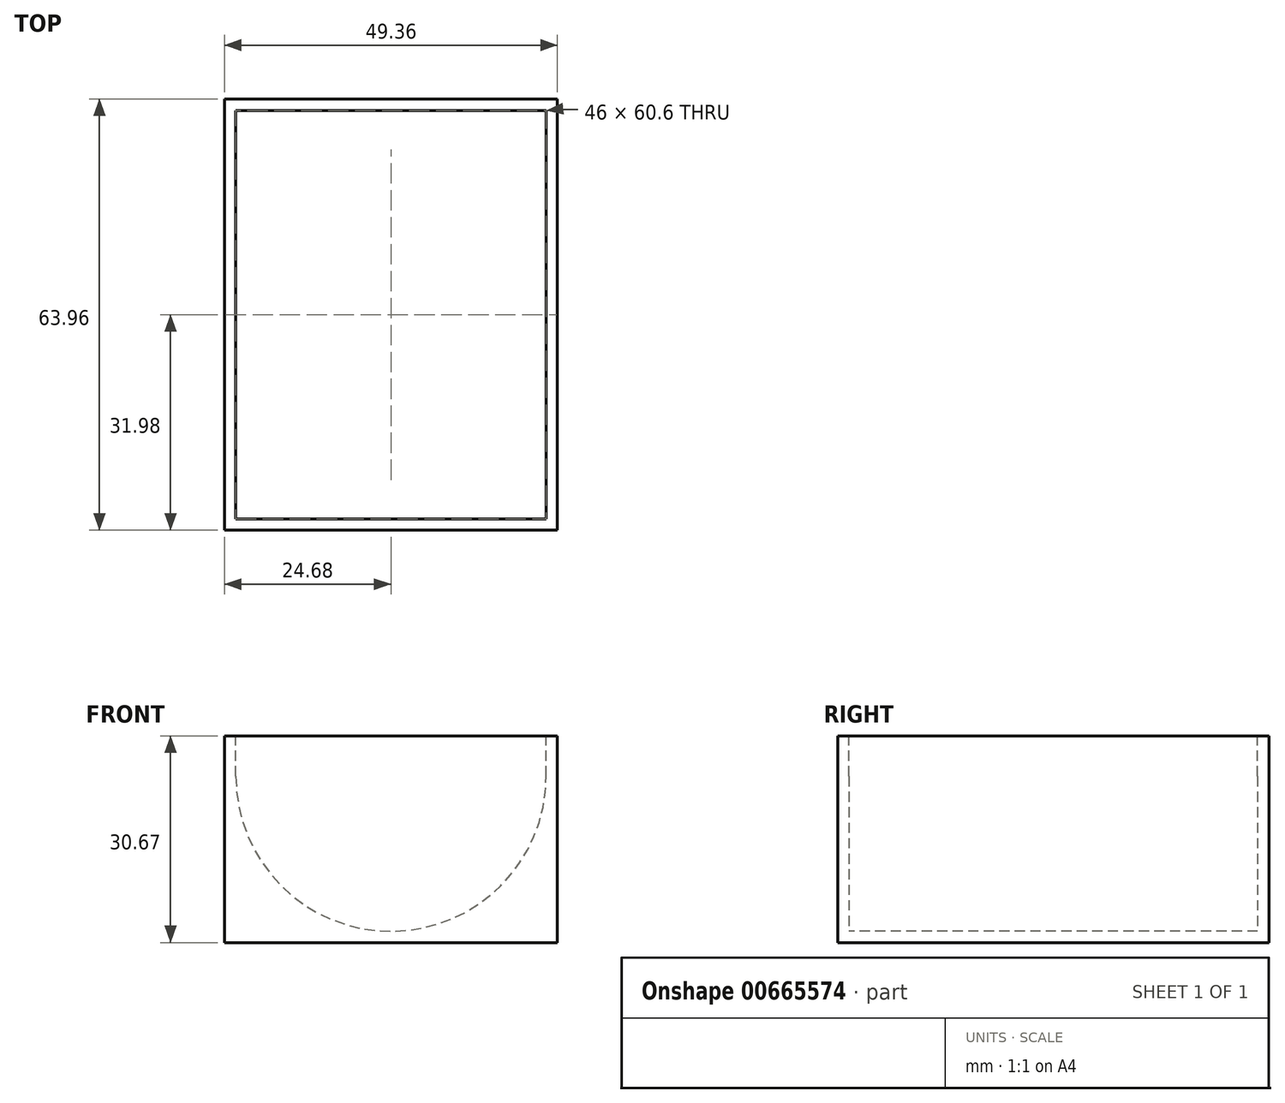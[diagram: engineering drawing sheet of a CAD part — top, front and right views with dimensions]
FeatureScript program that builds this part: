
annotation { "Feature Type Name" : "Feature", "Feature Type Description" : "" }
export const myFeature = defineFeature(function(context is Context, id is Id, definition is map)
    precondition{}
    {
        {
            assignVariable(context, id + "F0", {"name" : "stacklength", "anyValue" : 60.6});
        }
        {
            assignVariable(context, id + "F1", {"name" : "wall", "anyValue" : 1.68});
        }
        {
            var Q0;
            Q0=qCreatedBy(makeId("Front.planeOp"),FACE);
            var sketch = newSketch(context, id + "F2", { "sketchPlane" : qUnion([Q0])});
            skLineSegment(sketch, "E0.bottom", {"start": v(24.68, 5.99) * mm, "end": v(-24.68, 5.99) * mm});
            skLineSegment(sketch, "E0.top", {"start": v(24.68, -24.68) * mm, "end": v(-24.68, -24.68) * mm});
            skLineSegment(sketch, "E0.left", {"start": v(24.68, 5.99) * mm, "end": v(24.68, -24.68) * mm});
            skLineSegment(sketch, "E0.right", {"start": v(-24.68, 5.99) * mm, "end": v(-24.68, -24.68) * mm});
            skPoint(sketch, "E0.middle", {"position": v(0, -9.35) * mm});
            skSolve(sketch);
        }
        {
            var Q0;
            Q0=qCreatedBy(makeId("Front.planeOp"),FACE);
            var sketch = newSketch(context, id + "F3", { "sketchPlane" : qUnion([Q0])});
            skCircle(sketch, "E1", {"center": v(0, 0) * mm, "radius": 23 * mm});
            skLineSegment(sketch, "E2.bottom", {"start": v(-23, 0) * mm, "end": v(23, 0) * mm});
            skLineSegment(sketch, "E2.top", {"start": v(-23, 23) * mm, "end": v(23, 23) * mm});
            skLineSegment(sketch, "E2.left", {"start": v(-23, 0) * mm, "end": v(-23, 23) * mm});
            skLineSegment(sketch, "E2.right", {"start": v(23, 0) * mm, "end": v(23, 23) * mm});
            skSolve(sketch);
        }
        {
            var Q0;
            Q0 = qSketchRegion(id + "F2", true);
            extrude(context, id + "F4", {"entities" : qUnion([Q0]), "oppositeDirection" : true, "depth" : (getVariable(context, 'stacklength') + getVariable(context, 'wall')) * mm, "offsetDistance" : 25 * mm, "hasSecondDirection" : true, "secondDirectionOppositeDirection" : false, "secondDirectionDepth" : (getVariable(context, 'wall')) * mm});
        }
        {
            var Q0;
            Q0 = qSketchRegion(id + "F3", true);
            extrude(context, id + "F5", {"entities" : qUnion([Q0]), "operationType" : NewBodyOperationType.REMOVE, "oppositeDirection" : true, "depth" : getVariable(context, 'stacklength') * mm, "offsetDistance" : 25 * mm});
        }
    });
